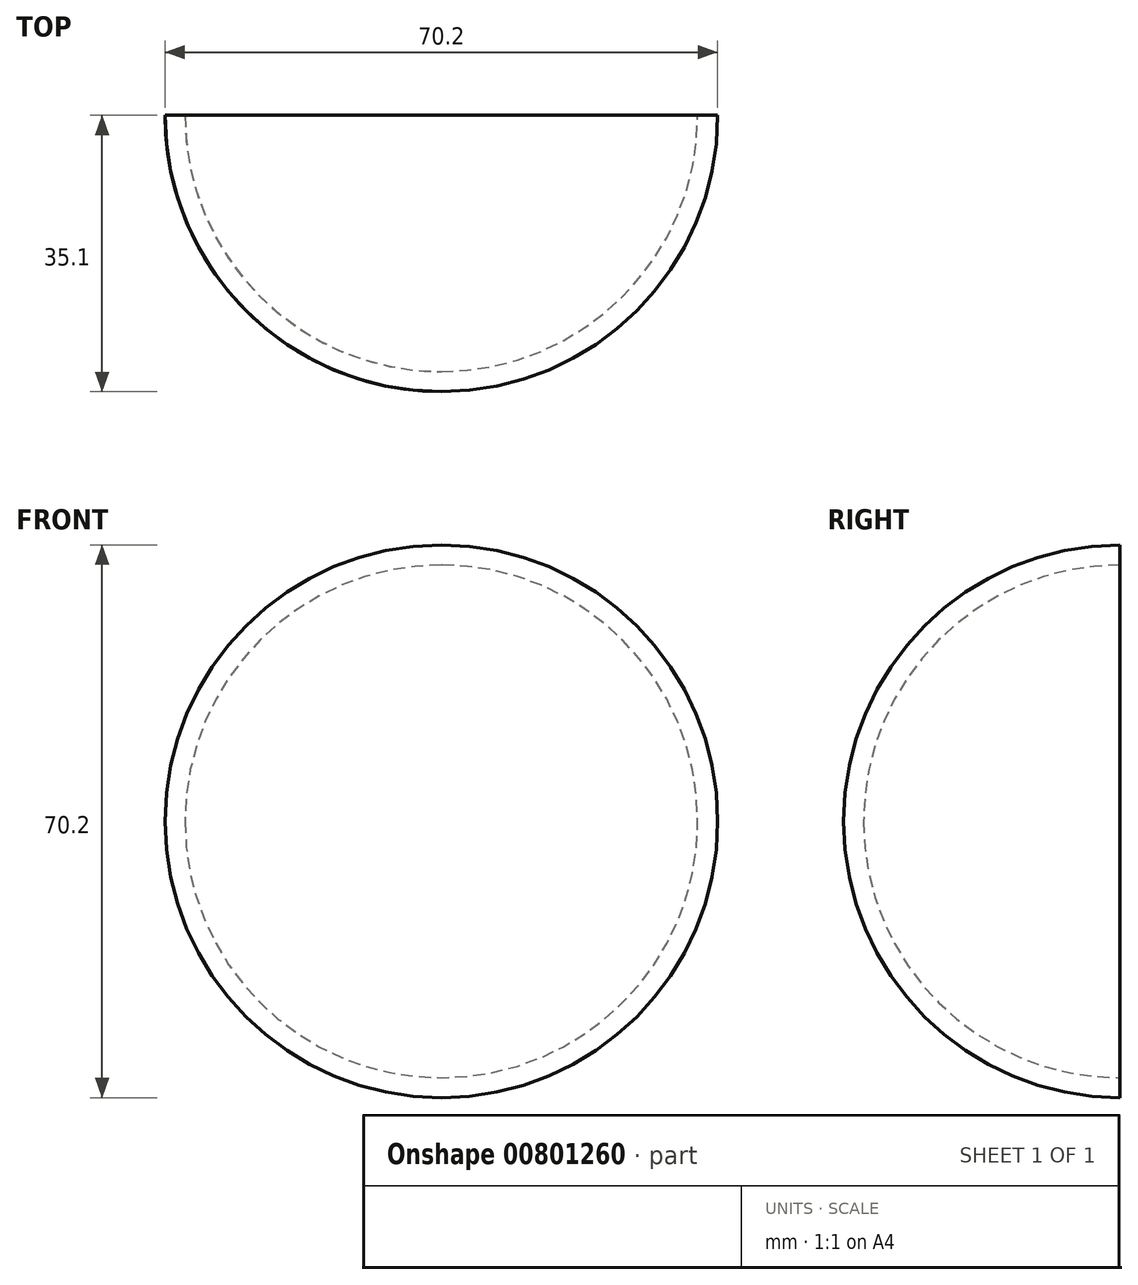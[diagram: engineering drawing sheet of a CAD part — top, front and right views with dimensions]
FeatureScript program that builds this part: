
annotation { "Feature Type Name" : "Feature", "Feature Type Description" : "" }
export const myFeature = defineFeature(function(context is Context, id is Id, definition is map)
    precondition{}
    {
        {
            var Q0;
            Q0=qCreatedBy(makeId("Top.planeOp"),FACE);
            var sketch = newSketch(context, id + "F0", { "sketchPlane" : qUnion([Q0])});
            skLineSegment(sketch, "E0", {"start": v(-35.1, 0) * mm, "end": v(35.1, 0) * mm});
            skArc(sketch, "E1", {"start": v(-35.1, 0) * mm, "mid": v(0, -35.1) * mm, "end": v(35.1, 0) * mm});
            skLineSegment(sketch, "E2", {"start": v(0, -35.1) * mm, "end": v(0, 0) * mm});
            skSolve(sketch);
        }
        {
            var Q0;
            {var subQ3=sQuery(id+"F0.wireOp",EDGE,"E2");Q0=makeQuery(id+"F0.imprint","IMPRINT",FACE,{"disambiguationData":[TD([[makeQuery(id+"F0.imprint","IMPRINT",EDGE,{"derivedFrom":subQ3}),1.0]])]});}
            var Q1;
            Q1=sQuery(id+"F0.wireOp",EDGE,"E2");
            revolve(context, id + "F1", {"surfaceOperationType" : NewSurfaceOperationType.NEW, "entities" : qUnion([Q0]), "axis" : qUnion([Q1]), "revolveType" : RevolveType.FULL});
        }
        {
            var Q0;
            Q0=makeQuery(id+"F1.opRevolve","SWEPT_FACE",FACE,{"disambiguationData":[OSD([sQuery(id+"F0.wireOp",EDGE,"E0")])]});
            shell(context, id + "F2", {"entities" : qUnion([Q0]), "thickness" : 2.54 * mm});
        }
    });
